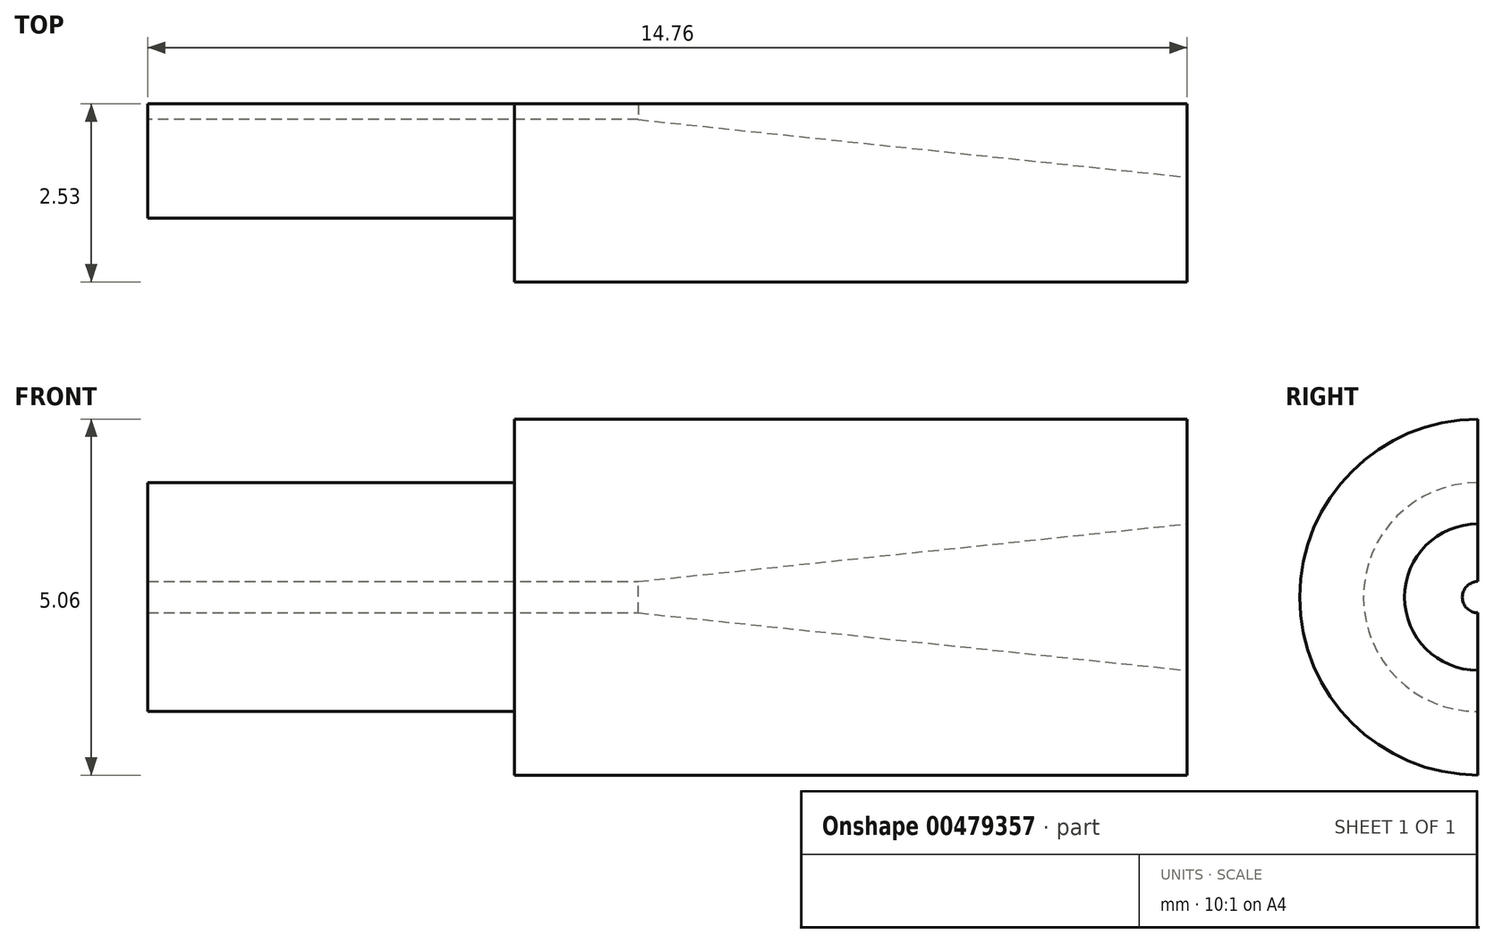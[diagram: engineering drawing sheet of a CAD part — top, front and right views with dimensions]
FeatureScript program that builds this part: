
annotation { "Feature Type Name" : "Feature", "Feature Type Description" : "" }
export const myFeature = defineFeature(function(context is Context, id is Id, definition is map)
    precondition{}
    {
        {
            var Q0;
            Q0=qCreatedBy(makeId("Front.planeOp"),FACE);
            var sketch = newSketch(context, id + "F0", { "sketchPlane" : qUnion([Q0])});
            skLineSegment(sketch, "E0", {"start": v(6.48, 2.53) * mm, "end": v(6.48, 1.04) * mm});
            skLineSegment(sketch, "E1", {"start": v(-8.28, 0.22) * mm, "end": v(-8.28, 1.63) * mm});
            skLineSegment(sketch, "E2", {"start": v(-8.28, 1.63) * mm, "end": v(-3.07, 1.63) * mm});
            skLineSegment(sketch, "E3", {"start": v(-3.07, 1.63) * mm, "end": v(-3.07, 2.53) * mm});
            skLineSegment(sketch, "E4", {"start": v(-3.07, 2.53) * mm, "end": v(6.48, 2.53) * mm});
            skLineSegment(sketch, "E5", {"start": v(-8.28, 0.22) * mm, "end": v(-1.31, 0.22) * mm});
            skLineSegment(sketch, "E6", {"start": v(-1.31, 0.22) * mm, "end": v(6.48, 1.04) * mm});
            skLineSegment(sketch, "E7", {"start": v(0, 0) * mm, "end": v(3.4, 0) * mm, "construction": true});
            skSolve(sketch);
        }
        {
            var Q0;
            Q0 = qSketchRegion(id + "F0", true);
            var Q1;
            Q1=sQuery(id+"F0.wireOp",EDGE,"E7");
            revolve(context, id + "F1", {"entities" : qUnion([Q0]), "axis" : qUnion([Q1]), "revolveType" : RevolveType.ONE_DIRECTION, "angle" : 180 * degree});
        }
    });
